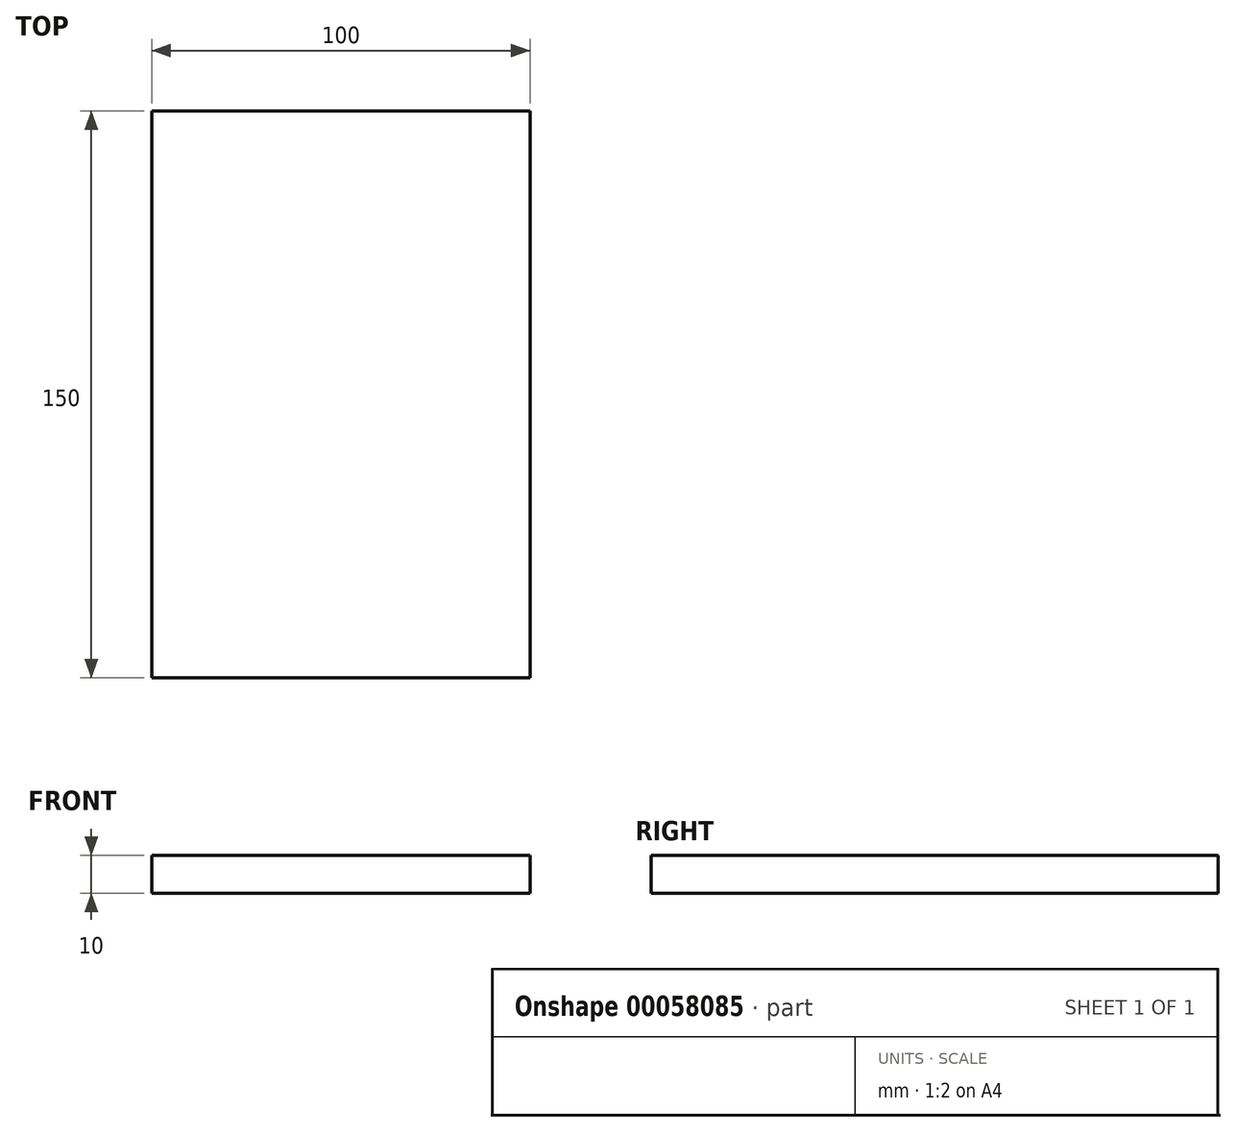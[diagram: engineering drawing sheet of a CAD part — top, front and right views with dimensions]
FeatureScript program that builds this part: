
annotation { "Feature Type Name" : "Feature", "Feature Type Description" : "" }
export const myFeature = defineFeature(function(context is Context, id is Id, definition is map)
    precondition{}
    {
        {
            var Q0;
            Q0=qCreatedBy(makeId("Top.planeOp"),FACE);
            var sketch = newSketch(context, id + "F0", { "sketchPlane" : qUnion([Q0])});
            skLineSegment(sketch, "E0.bottom", {"start": v(-55.77, -49.97) * mm, "end": v(44.23, -49.97) * mm});
            skLineSegment(sketch, "E0.top", {"start": v(-55.77, 100.03) * mm, "end": v(44.23, 100.03) * mm});
            skLineSegment(sketch, "E0.left", {"start": v(-55.77, -49.97) * mm, "end": v(-55.77, 100.03) * mm});
            skLineSegment(sketch, "E0.right", {"start": v(44.23, -49.97) * mm, "end": v(44.23, 100.03) * mm});
            skSolve(sketch);
        }
        {
            var Q0;
            Q0 = qSketchRegion(id + "F0", true);
            var Q1;
            Q1=makeQuery(id+"F0.imprint","IMPRINT",FACE,{"disambiguationData":[TD([[makeQuery(id+"F0.imprint","IMPRINT",EDGE,{"derivedFrom":sQuery(id+"F0.wireOp",EDGE,"E0.bottom")}),1.0]])]});
            extrude(context, id + "F1", {"entities" : qUnion([Q0, Q1]), "depth" : 10 * mm});
        }
    });
